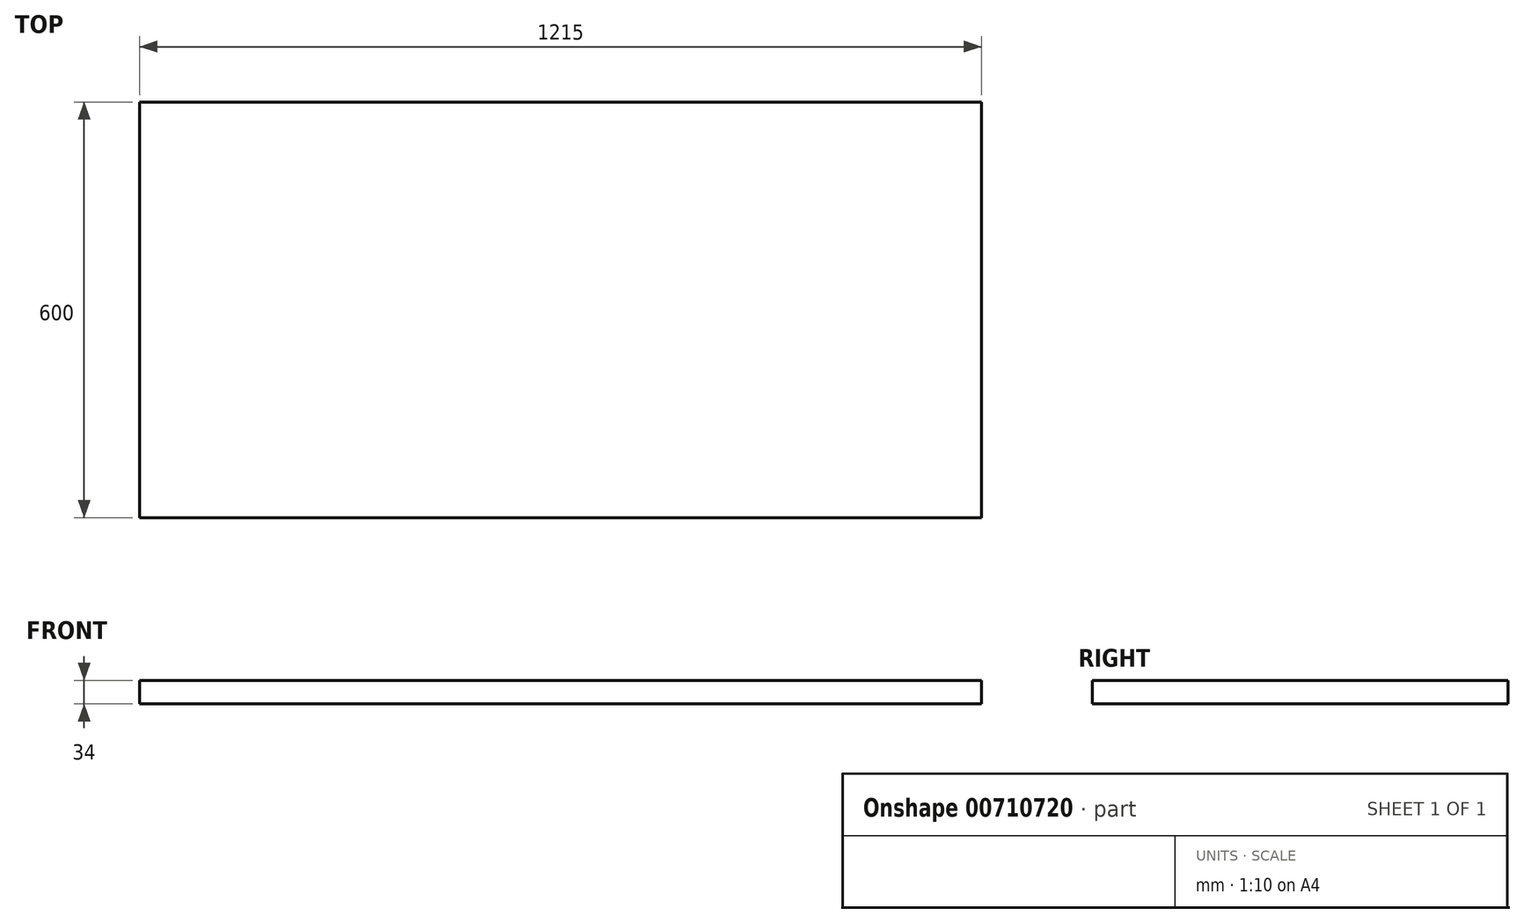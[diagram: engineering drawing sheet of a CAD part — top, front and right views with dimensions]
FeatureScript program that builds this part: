
annotation { "Feature Type Name" : "Feature", "Feature Type Description" : "" }
export const myFeature = defineFeature(function(context is Context, id is Id, definition is map)
    precondition{}
    {
        {
            var Q0;
            Q0=qCreatedBy(makeId("Top.planeOp"),FACE);
            var sketch = newSketch(context, id + "F0", { "sketchPlane" : qUnion([Q0])});
            skLineSegment(sketch, "E0", {"start": v(0, 0) * mm, "end": v(-1215, 0) * mm});
            skLineSegment(sketch, "E1", {"start": v(-1215, 0) * mm, "end": v(-1215, -600) * mm});
            skLineSegment(sketch, "E2", {"start": v(-1215, -600) * mm, "end": v(0, -600) * mm});
            skLineSegment(sketch, "E3", {"start": v(0, -600) * mm, "end": v(0, 0) * mm});
            skSolve(sketch);
        }
        {
            var Q0;
            Q0 = qSketchRegion(id + "F0", true);
            extrude(context, id + "F1", {"entities" : qUnion([Q0]), "depth" : 34 * mm, "offsetDistance" : 25 * mm});
        }
    });
